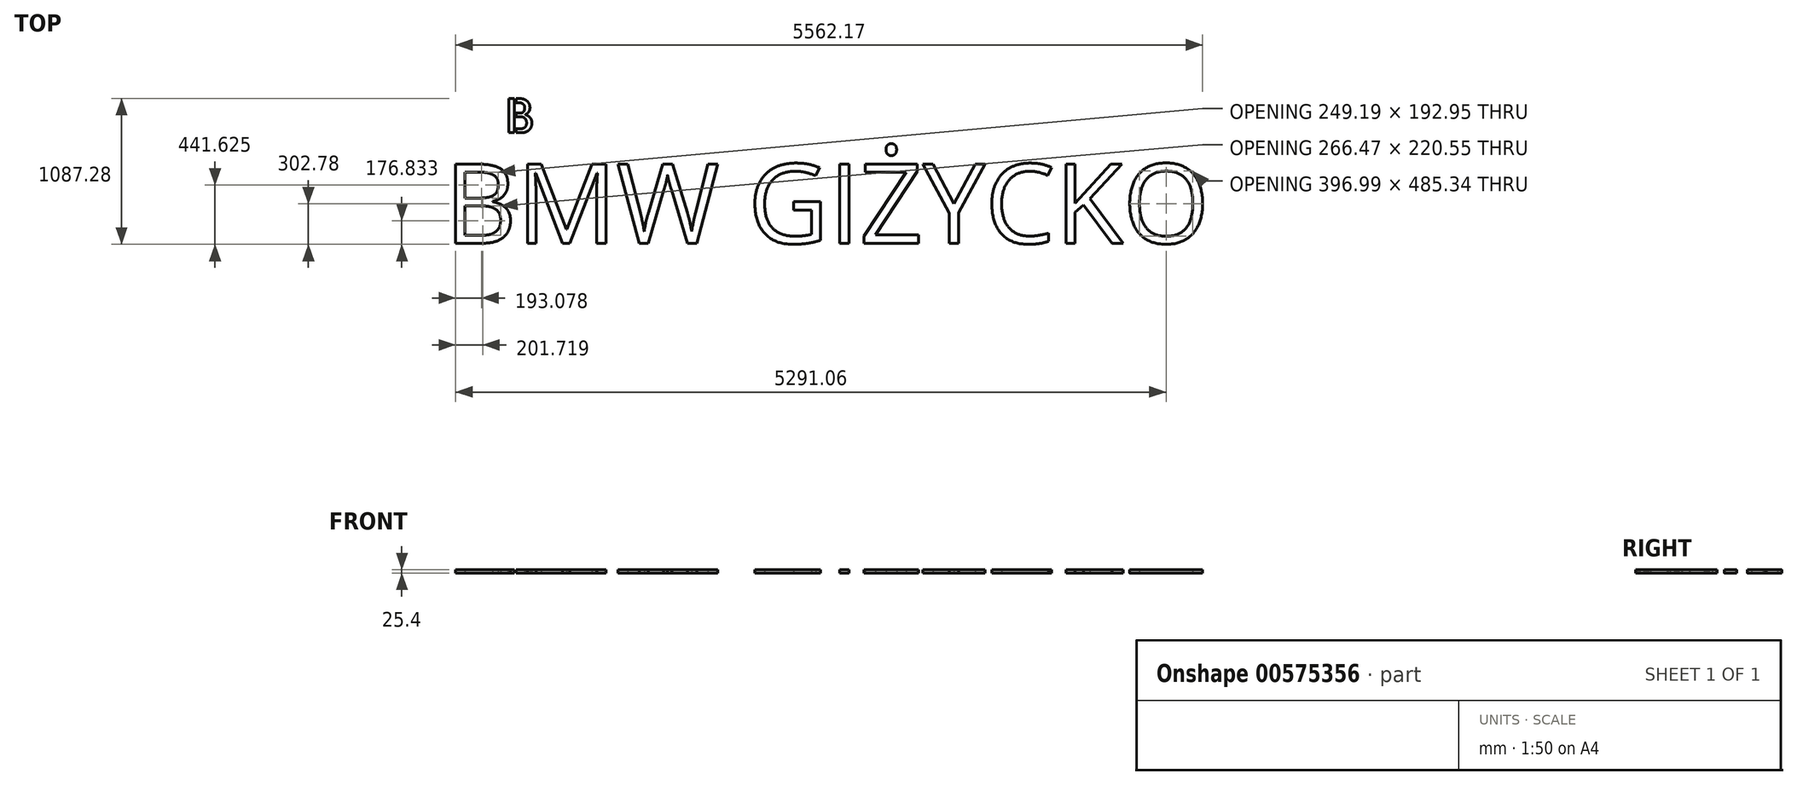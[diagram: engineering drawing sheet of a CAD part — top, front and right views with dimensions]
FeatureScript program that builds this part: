
annotation { "Feature Type Name" : "Feature", "Feature Type Description" : "" }
export const myFeature = defineFeature(function(context is Context, id is Id, definition is map)
    precondition{}
    {
        {
            var Q0;
            Q0=qCreatedBy(makeId("Top.planeOp"),FACE);
            var sketch = newSketch(context, id + "F0", { "sketchPlane" : qUnion([Q0])});
            skText(sketch, "E0", { "text": "BMW GIŻYCKO", "fontName": "OpenSans-Regular.ttf"});
            skText(sketch, "E1", { "text": "B", "fontName": "AllertaStencil-Regular.ttf"});
            const initialGuessF0  = {"E0": [-5.6967, 0, 1, 0, 0.59433], "E1": [-5.25387, 0.82333, 1, 0, 0.25593]};
            skSetInitialGuess(sketch, initialGuessF0);
            skSolve(sketch);
        }
        {
            var Q0;
            Q0 = qSketchRegion(id + "F0", true);
            extrude(context, id + "F1", {"entities" : qUnion([Q0]), "depth" : 25.4 * mm, "offsetDistance" : 25.4 * mm});
        }
    });
